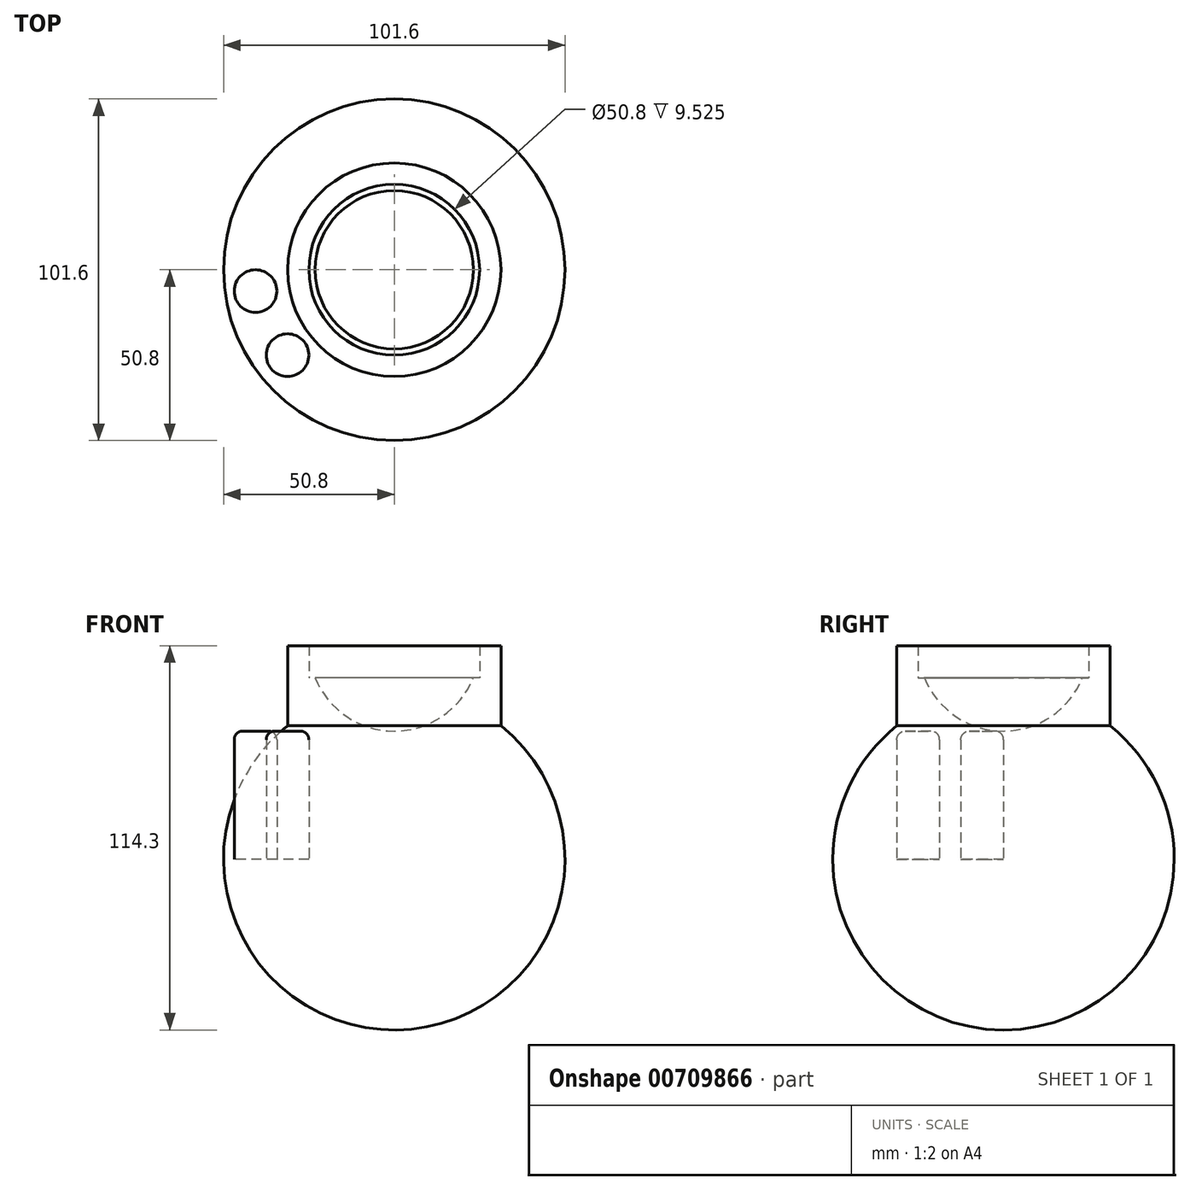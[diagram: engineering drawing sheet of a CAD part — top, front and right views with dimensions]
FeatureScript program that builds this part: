
annotation { "Feature Type Name" : "Feature", "Feature Type Description" : "" }
export const myFeature = defineFeature(function(context is Context, id is Id, definition is map)
    precondition{}
    {
        {
            var Q0;
            Q0=qCreatedBy(makeId("Top.planeOp"),FACE);
            var sketch = newSketch(context, id + "F0", { "sketchPlane" : qUnion([Q0])});
            skLineSegment(sketch, "E0", {"start": v(0, -50.8) * mm, "end": v(0, 50.8) * mm});
            skArc(sketch, "E1", {"start": v(0.17, -50.8) * mm, "mid": v(50.8, 0.08) * mm, "end": v(0, 50.8) * mm});
            skArc(sketch, "E2", {"start": v(0, -50.8) * mm, "mid": v(0.08, -50.8) * mm, "end": v(0.17, -50.8) * mm});
            skSolve(sketch);
        }
        {
            var Q0;
            Q0=makeQuery(id+"F0.imprint","IMPRINT",FACE,{"disambiguationData":[TD([[makeQuery(id+"F0.imprint","IMPRINT",EDGE,{"derivedFrom":sQuery(id+"F0.wireOp",EDGE,"E0")}),-1.0]])]});
            var Q1;
            Q1=sQuery(id+"F0.wireOp",EDGE,"E0");
            revolve(context, id + "F1", {"surfaceOperationType" : NewSurfaceOperationType.NEW, "entities" : qUnion([Q0]), "axis" : qUnion([Q1]), "revolveType" : RevolveType.FULL});
        }
        {
            var Q0;
            Q0=qCreatedBy(makeId("Top.planeOp"),FACE);
            var sketch = newSketch(context, id + "F2", { "sketchPlane" : qUnion([Q0])});
            skCircle(sketch, "E3", {"center": v(0, 0) * mm, "radius": 31.75 * mm});
            skCircle(sketch, "E4", {"center": v(0, 0) * mm, "radius": 25.4 * mm});
            skCircle(sketch, "E5", {"center": v(-31.75, -25.4) * mm, "radius": 6.35 * mm});
            skCircle(sketch, "E6", {"center": v(-41.28, -6.35) * mm, "radius": 6.35 * mm});
            skSolve(sketch);
        }
        {
            var Q0;
            Q0=makeQuery(id+"F2.imprint","IMPRINT",FACE,{"disambiguationData":[TD([[makeQuery(id+"F2.imprint","IMPRINT",EDGE,{"derivedFrom":sQuery(id+"F2.wireOp",EDGE,"E3")}),1.0]])]});
            extrude(context, id + "F3", {"entities" : qUnion([Q0]), "depth" : 63.5 * mm, "offsetDistance" : 25.4 * mm});
        }
        {
            var Q0;
            Q0=makeQuery(id+"F2.imprint","IMPRINT",FACE,{"disambiguationData":[TD([[makeQuery(id+"F2.imprint","IMPRINT",EDGE,{"derivedFrom":sQuery(id+"F2.wireOp",EDGE,"E4")}),1.0]])]});
            extrude(context, id + "F4", {"entities" : qUnion([Q0]), "operationType" : NewBodyOperationType.ADD, "depth" : 53.97 * mm, "offsetDistance" : 25.4 * mm});
        }
        {
            var Q0;
            Q0=makeQuery(id+"F3.opExtrude","CAP_FACE",FACE,{"disambiguationData":[OSD([sQuery(id+"F2.wireOp",EDGE,"E3"),sQuery(id+"F2.wireOp",EDGE,"E4")])],"isStart":false});
            var sketch = newSketch(context, id + "F5", { "sketchPlane" : qUnion([Q0])});
            skLineSegment(sketch, "E7", {"start": v(0, 25.4) * mm, "end": v(0, -25.4) * mm});
            skArc(sketch, "E8", {"start": v(0, -25.4) * mm, "mid": v(25.4, 0) * mm, "end": v(0, 25.4) * mm});
            skSolve(sketch);
        }
        {
            var Q0;
            Q0=makeQuery(id+"F5.imprint","IMPRINT",FACE,{"disambiguationData":[TD([[makeQuery(id+"F5.imprint","IMPRINT",EDGE,{"derivedFrom":sQuery(id+"F5.wireOp",EDGE,"E7")}),1.0]])]});
            var Q1;
            Q1=sQuery(id+"F5.wireOp",EDGE,"E7");
            revolve(context, id + "F6", {"operationType" : NewBodyOperationType.REMOVE, "surfaceOperationType" : NewSurfaceOperationType.NEW, "entities" : qUnion([Q0]), "axis" : qUnion([Q1]), "revolveType" : RevolveType.FULL, "oppositeDirection" : true});
        }
        {
            var Q0;
            Q0=makeQuery(id+"F2.imprint","IMPRINT",FACE,{"disambiguationData":[TD([[makeQuery(id+"F2.imprint","IMPRINT",EDGE,{"derivedFrom":sQuery(id+"F2.wireOp",EDGE,"E6")}),1.0]])]});
            extrude(context, id + "F7", {"entities" : qUnion([Q0]), "depth" : 38.1 * mm, "offsetDistance" : 25.4 * mm});
        }
        {
            var Q0;
            Q0=makeQuery(id+"F2.imprint","IMPRINT",FACE,{"disambiguationData":[TD([[makeQuery(id+"F2.imprint","IMPRINT",EDGE,{"derivedFrom":sQuery(id+"F2.wireOp",EDGE,"E5")}),1.0]])]});
            extrude(context, id + "F8", {"entities" : qUnion([Q0]), "depth" : 38.1 * mm, "offsetDistance" : 25.4 * mm});
        }
        {
            var Q0;
            Q0=makeQuery(id+"F7.opExtrude","CAP_EDGE",EDGE,{"disambiguationData":[OSD([sQuery(id+"F2.wireOp",EDGE,"E6")])],"isStart":false});
            var Q1;
            Q1=makeQuery(id+"F8.opExtrude","CAP_EDGE",EDGE,{"disambiguationData":[OSD([sQuery(id+"F2.wireOp",EDGE,"E5")])],"isStart":false});
            fillet(context, id + "F9", {"entities" : qUnion([Q0, Q1]), "radius" : 2.54 * mm, "tangentPropagation" : true, "allowEdgeOverflow" : false});
        }
    });
